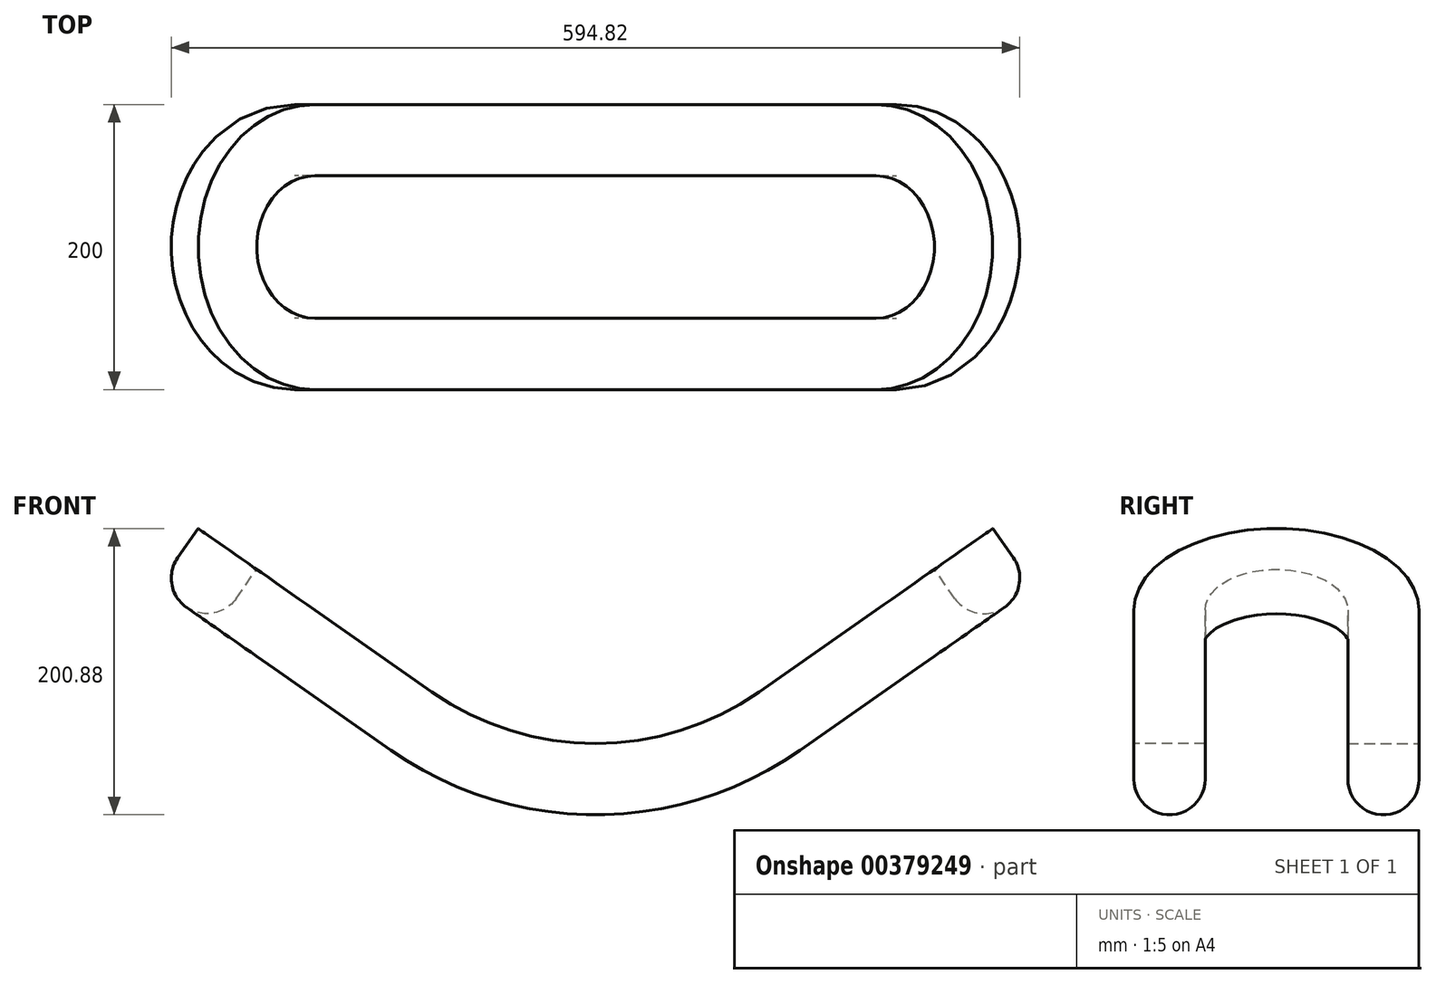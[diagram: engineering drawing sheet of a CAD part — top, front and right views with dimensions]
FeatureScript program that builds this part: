
annotation { "Feature Type Name" : "Feature", "Feature Type Description" : "" }
export const myFeature = defineFeature(function(context is Context, id is Id, definition is map)
    precondition{}
    {
        {
            var Q0;
            Q0=qCreatedBy(makeId("Front.planeOp"),FACE);
            var sketch = newSketch(context, id + "F0", { "sketchPlane" : qUnion([Q0])});
            skArc(sketch, "E0", {"start": v(0, 0) * mm, "mid": v(60.14, 9.26) * mm, "end": v(114.72, 36.17) * mm});
            skLineSegment(sketch, "E1", {"start": v(0, 200) * mm, "end": v(114.72, 36.17) * mm, "construction": true});
            skLineSegment(sketch, "E2", {"start": v(114.72, 36.17) * mm, "end": v(196.63, 93.53) * mm});
            skLineSegment(sketch, "E3", {"start": v(0, 200) * mm, "end": v(0, 0) * mm, "construction": true});
            skSolve(sketch);
        }
        {
            var Q0;
            Q0=sQuery(id+"F0.wireOp",EDGE,"E2");
            var Q1;
            Q1=sQuery(id+"F0.wireOp",EDGE,"E0");
            extrude(context, id + "F1", {"bodyType" : ToolBodyType.SURFACE, "surfaceEntities" : qUnion([Q0, Q1]), "depth" : 50 * mm});
        }
        {
            var Q0;
            Q0=qCreatedBy(makeId("Right.planeOp"),FACE);
            var sketch = newSketch(context, id + "F2", { "sketchPlane" : qUnion([Q0])});
            skLineSegment(sketch, "E4.bottom", {"start": v(-50, 0) * mm, "end": v(0, 0) * mm});
            skLineSegment(sketch, "E4.left", {"start": v(-50, 0) * mm, "end": v(-50, -25) * mm});
            skLineSegment(sketch, "E4.right", {"start": v(0, 0) * mm, "end": v(0, -25) * mm});
            skArc(sketch, "E5", {"start": v(-50, -25) * mm, "mid": v(-25, -50) * mm, "end": v(0, -25) * mm});
            skSolve(sketch);
        }
        {
            var Q0;
            Q0=makeQuery(id+"F1.opExtrude","CAP_VERTEX",VERTEX,{"disambiguationData":[OSD([sQuery(id+"F0.wireOp",VERTEX,"E2.end")])],"isStart":false});
            var Q1;
            Q1=makeQuery(id+"F1.opExtrude","CAP_VERTEX",VERTEX,{"disambiguationData":[OSD([sQuery(id+"F0.wireOp",VERTEX,"E2.end")])],"isStart":true});
            var Q2;
            Q2=makeQuery(id+"F1.opExtrude","CAP_VERTEX",VERTEX,{"disambiguationData":[OSD([sQuery(id+"F0.wireOp",VERTEX,"E0.end")])],"isStart":true});
            cPlane(context, id + "F3", {"entities" : qUnion([Q0, Q1, Q2]), "cplaneType" : CPlaneType.THREE_POINT, "offset" : 25 * mm, "width" : 150 * mm, "height" : 150 * mm});
        }
        {
            var Q0;
            Q0=qCreatedBy(id+"F3.planeOp",FACE);
            var sketch = newSketch(context, id + "F4", { "sketchPlane" : qUnion([Q0])});
            skArc(sketch, "E6", {"start": v(214.72, 0) * mm, "mid": v(250.07, -14.64) * mm, "end": v(264.72, -50) * mm});
            skArc(sketch, "E7", {"start": v(214.72, 50) * mm, "mid": v(285.43, 20.71) * mm, "end": v(314.72, -50) * mm});
            skLineSegment(sketch, "E8", {"start": v(264.72, -50) * mm, "end": v(314.72, -50) * mm});
            skSolve(sketch);
        }
        {
            var Q0;
            Q0=makeQuery(id+"F2.imprint","IMPRINT",FACE,{"disambiguationData":[TD([[makeQuery(id+"F2.imprint","IMPRINT",EDGE,{"derivedFrom":sQuery(id+"F2.wireOp",EDGE,"E4.bottom")}),-1.0]])]});
            var Q1;
            Q1=makeQuery(id+"F1.opExtrude","CAP_EDGE",EDGE,{"disambiguationData":[OSD([sQuery(id+"F0.wireOp",EDGE,"E0")])],"isStart":false});
            var Q2;
            Q2=makeQuery(id+"F1.opExtrude","CAP_EDGE",EDGE,{"disambiguationData":[OSD([sQuery(id+"F0.wireOp",EDGE,"E2")])],"isStart":false});
            var Q3;
            Q3=sQuery(id+"F4.wireOp",EDGE,"E7");
            sweep(context, id + "F5", {"profiles" : qUnion([Q0]), "path" : qUnion([Q1, Q2, Q3])});
        }
        {
            var Q0;
            Q0=makeQuery(id+"F5.opSweep","CAP_EDGE",EDGE,{"disambiguationData":[OSD([sQuery(id+"F2.wireOp",EDGE,"E5"),sQuery(id+"F4.wireOp",VERTEX,"E7.end")])],"isStart":false});
            cPoint(context, id + "F6", {"entities" : qUnion([Q0]), "parameter" : 0.5});
        }
        {
            var Q0;
            Q0=makeQuery(id+"F5.opSweep","CAP_VERTEX",VERTEX,{"disambiguationData":[OSD([sQuery(id+"F2.wireOp",EDGE,"E4.bottom"),sQuery(id+"F2.wireOp",EDGE,"E4.left"),sQuery(id+"F4.wireOp",EDGE,"E7")])],"isStart":false});
            var Q1;
            Q1=makeQuery(id+"F5.opSweep","CAP_VERTEX",VERTEX,{"disambiguationData":[OSD([sQuery(id+"F2.wireOp",EDGE,"E4.bottom"),sQuery(id+"F2.wireOp",EDGE,"E4.right"),sQuery(id+"F4.wireOp",EDGE,"E7")])],"isStart":false});
            var Q2;
            Q2 = qCreatedBy(id + "F6" ,VERTEX);
            cPlane(context, id + "F7", {"entities" : qUnion([Q0, Q1, Q2]), "cplaneType" : CPlaneType.THREE_POINT, "offset" : 25 * mm, "width" : 150 * mm, "height" : 150 * mm});
        }
        {
            var Q0;
            Q0=makeQuery(id+"F5.opSweep","SWEPT_BODY",BODY,{"disambiguationData":[OSD([sQuery(id+"F2.wireOp",EDGE,"E4.bottom"),sQuery(id+"F2.wireOp",EDGE,"E4.left"),sQuery(id+"F2.wireOp",EDGE,"E4.right"),sQuery(id+"F2.wireOp",EDGE,"E5"),sQuery(id+"F4.wireOp",EDGE,"E7")])]});
            var Q1;
            Q1=qCreatedBy(id+"F7.planeOp",FACE);
            mirror(context, id + "F8", {"operationType" : NewBodyOperationType.ADD, "entities" : qUnion([Q0]), "mirrorPlane" : qUnion([Q1])});
        }
        {
            var Q0;
            Q0=makeQuery(id+"F5.opSweep","SWEPT_BODY",BODY,{"disambiguationData":[OSD([sQuery(id+"F2.wireOp",EDGE,"E4.bottom"),sQuery(id+"F2.wireOp",EDGE,"E4.left"),sQuery(id+"F2.wireOp",EDGE,"E4.right"),sQuery(id+"F2.wireOp",EDGE,"E5"),sQuery(id+"F4.wireOp",EDGE,"E7")])]});
            var Q1;
            Q1=qCreatedBy(makeId("Right.planeOp"),FACE);
            mirror(context, id + "F9", {"operationType" : NewBodyOperationType.ADD, "entities" : qUnion([Q0]), "mirrorPlane" : qUnion([Q1])});
        }
    });
